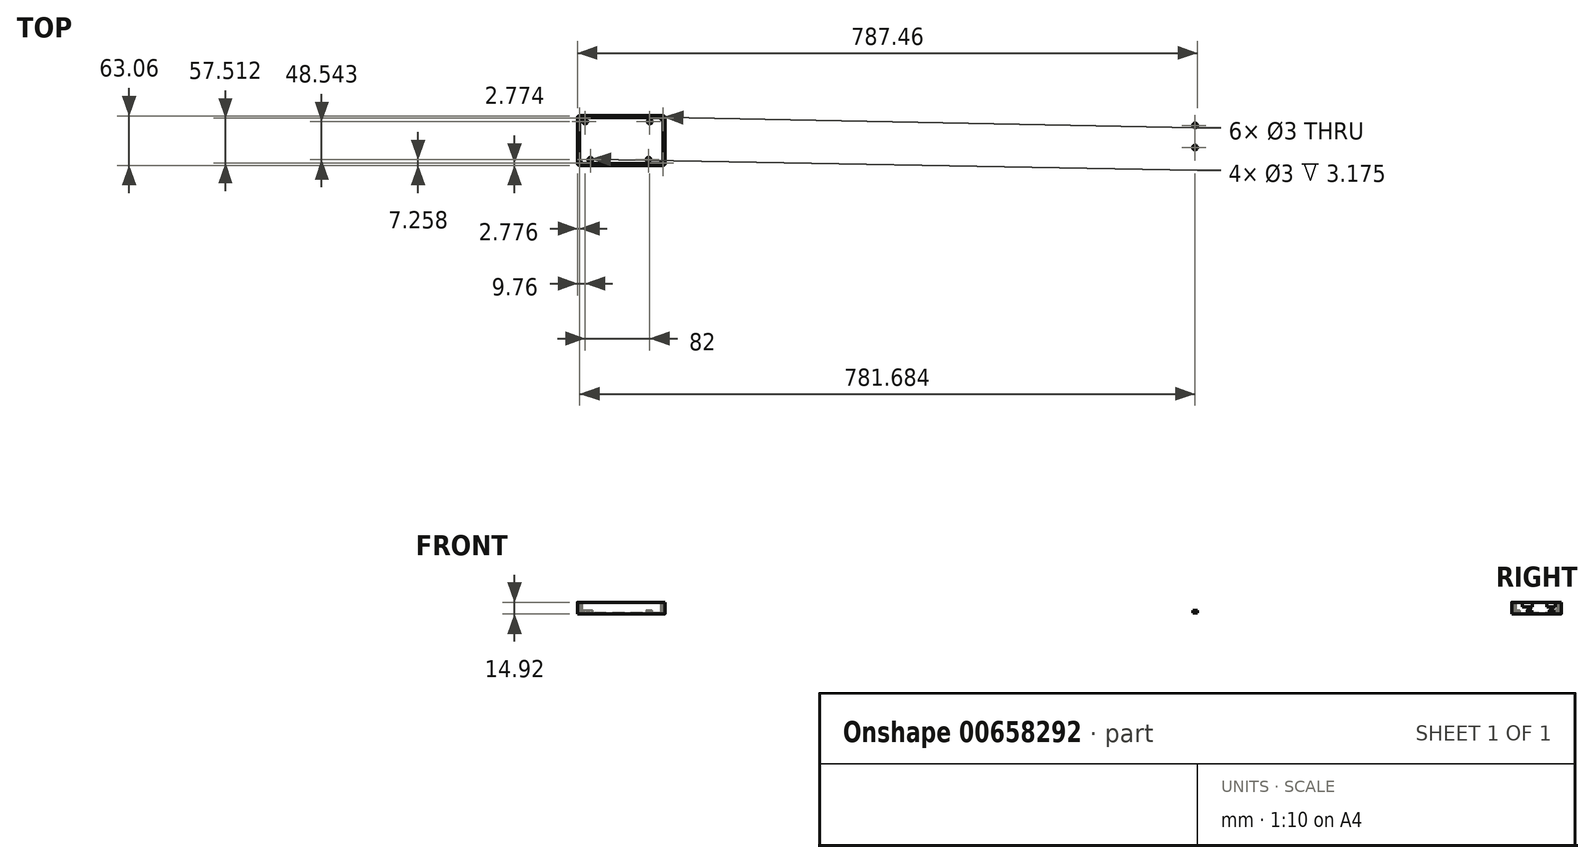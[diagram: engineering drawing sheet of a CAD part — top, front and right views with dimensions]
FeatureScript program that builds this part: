
annotation { "Feature Type Name" : "Feature", "Feature Type Description" : "" }
export const myFeature = defineFeature(function(context is Context, id is Id, definition is map)
    precondition{}
    {
        {
            var Q0;
            Q0=qCreatedBy(makeId("Top.planeOp"),FACE);
            var sketch = newSketch(context, id + "F0", { "sketchPlane" : qUnion([Q0])});
            skLineSegment(sketch, "E0.bottom", {"start": v(50.8, 26.77) * mm, "end": v(-50.8, 26.77) * mm});
            skLineSegment(sketch, "E0.top", {"start": v(50.8, -26.77) * mm, "end": v(-50.8, -26.77) * mm});
            skLineSegment(sketch, "E0.left", {"start": v(50.8, 26.77) * mm, "end": v(50.8, -26.77) * mm});
            skLineSegment(sketch, "E0.right", {"start": v(-50.8, 26.77) * mm, "end": v(-50.8, -26.77) * mm});
            skPoint(sketch, "E0.middle", {"position": v(0, 0) * mm});
            skSolve(sketch);
        }
        {
            var Q0;
            Q0=qCreatedBy(makeId("Top.planeOp"),FACE);
            var sketch = newSketch(context, id + "F1", { "sketchPlane" : qUnion([Q0])});
            skLineSegment(sketch, "E1.bottom", {"start": v(55.56, 31.53) * mm, "end": v(-55.56, 31.53) * mm});
            skLineSegment(sketch, "E1.top", {"start": v(55.56, -31.53) * mm, "end": v(-55.56, -31.53) * mm});
            skLineSegment(sketch, "E1.left", {"start": v(55.56, 31.53) * mm, "end": v(55.56, -31.53) * mm});
            skLineSegment(sketch, "E1.right", {"start": v(-55.56, 31.53) * mm, "end": v(-55.56, -31.53) * mm});
            skPoint(sketch, "E1.middle", {"position": v(0, 0) * mm});
            skLineSegment(sketch, "E2.bottom", {"start": v(53.97, 29.95) * mm, "end": v(-53.98, 29.95) * mm, "construction": true});
            skLineSegment(sketch, "E2.top", {"start": v(53.98, -29.95) * mm, "end": v(-53.97, -29.95) * mm, "construction": true});
            skLineSegment(sketch, "E2.left", {"start": v(53.97, 29.95) * mm, "end": v(53.98, -29.95) * mm, "construction": true});
            skLineSegment(sketch, "E2.right", {"start": v(-53.98, 29.95) * mm, "end": v(-53.97, -29.95) * mm, "construction": true});
            skSolve(sketch);
        }
        {
            var Q0;
            Q0=makeQuery(id+"F1.imprint","IMPRINT",FACE,{"disambiguationData":[TD([[makeQuery(id+"F1.imprint","IMPRINT",EDGE,{"derivedFrom":sQuery(id+"F1.wireOp",EDGE,"E1.bottom")}),1.0]])]});
            extrude(context, id + "F2", {"entities" : qUnion([Q0]), "depth" : 1.59 * mm, "offsetDistance" : 25.4 * mm});
        }
        {
            var Q0;
            Q0=makeQuery(id+"F2.opExtrude","CAP_FACE",FACE,{"disambiguationData":[OSD([sQuery(id+"F1.wireOp",EDGE,"E1.bottom"),sQuery(id+"F1.wireOp",EDGE,"E1.top"),sQuery(id+"F1.wireOp",EDGE,"E1.left"),sQuery(id+"F1.wireOp",EDGE,"E1.right")])],"isStart":false});
            var sketch = newSketch(context, id + "F3", { "sketchPlane" : qUnion([Q0])});
            skLineSegment(sketch, "E3.bottom", {"start": v(55.56, 31.53) * mm, "end": v(-55.56, 31.53) * mm});
            skLineSegment(sketch, "E3.top", {"start": v(55.56, -31.53) * mm, "end": v(-55.56, -31.53) * mm});
            skLineSegment(sketch, "E3.left", {"start": v(55.56, 31.53) * mm, "end": v(55.56, -31.53) * mm});
            skLineSegment(sketch, "E3.right", {"start": v(-55.56, 31.53) * mm, "end": v(-55.56, -31.53) * mm});
            skPoint(sketch, "E3.middle", {"position": v(0, 0) * mm});
            skLineSegment(sketch, "E4.left", {"start": v(53.18, 25.98) * mm, "end": v(53.18, -25.98) * mm});
            skLineSegment(sketch, "E4.right", {"start": v(-53.18, 25.98) * mm, "end": v(-53.18, -25.98) * mm});
            skArc(sketch, "E5", {"start": v(-52.78, 25.98) * mm, "mid": v(-50.82, 26.8) * mm, "end": v(-50, 28.76) * mm});
            skCircle(sketch, "E6", {"center": v(-52.78, 28.76) * mm, "radius": 1.5 * mm});
            skLineSegment(sketch, "E7", {"start": v(-50, 28.76) * mm, "end": v(-50, 29.15) * mm});
            skLineSegment(sketch, "E8", {"start": v(-52.78, 25.98) * mm, "end": v(-53.18, 25.98) * mm});
            skLineSegment(sketch, "E9", {"start": v(-55.56, 31.53) * mm, "end": v(-50.82, 26.8) * mm, "construction": true});
            skPoint(sketch, "E10", {"position": v(-53.2, 29.16) * mm});
            skPoint(sketch, "E11.orphan", {"position": v(-53.18, 37.1) * mm});
            skCircle(sketch, "E12.MirrorC", {"center": v(-52.78, -28.76) * mm, "radius": 1.5 * mm});
            skLineSegment(sketch, "E13.MirrorCS", {"start": v(-52.78, -25.98) * mm, "end": v(-53.18, -25.98) * mm});
            skArc(sketch, "E14.MirrorCS", {"start": v(-52.78, -25.98) * mm, "mid": v(-50.82, -26.8) * mm, "end": v(-50, -28.76) * mm});
            skLineSegment(sketch, "E15.MirrorCS", {"start": v(-50, -28.76) * mm, "end": v(-50, -29.15) * mm});
            skCircle(sketch, "E16.MirrorC", {"center": v(52.78, 28.76) * mm, "radius": 1.5 * mm});
            skLineSegment(sketch, "E17.MirrorCS", {"start": v(50, 28.76) * mm, "end": v(50, 29.15) * mm});
            skArc(sketch, "E18.MirrorCS", {"start": v(52.78, 25.98) * mm, "mid": v(50.82, 26.8) * mm, "end": v(50, 28.76) * mm});
            skLineSegment(sketch, "E19.MirrorCS", {"start": v(52.78, 25.98) * mm, "end": v(53.18, 25.98) * mm});
            skCircle(sketch, "E20.MirrorC", {"center": v(52.78, -28.76) * mm, "radius": 1.5 * mm});
            skLineSegment(sketch, "E21.MirrorCS", {"start": v(52.78, -25.98) * mm, "end": v(53.18, -25.98) * mm});
            skArc(sketch, "E22.MirrorCS", {"start": v(52.78, -25.98) * mm, "mid": v(50.82, -26.8) * mm, "end": v(50, -28.76) * mm});
            skLineSegment(sketch, "E23.MirrorCS", {"start": v(50, -28.76) * mm, "end": v(50, -29.15) * mm});
            skPoint(sketch, "E24.orphan", {"position": v(-53.18, -36.9) * mm});
            skLineSegment(sketch, "E25.trimOffspring", {"start": v(50, -29.15) * mm, "end": v(-50, -29.15) * mm});
            skPoint(sketch, "E26.orphan", {"position": v(53.18, -37.1) * mm});
            skLineSegment(sketch, "E27.trimOffspring", {"start": v(50, 29.15) * mm, "end": v(-50, 29.15) * mm});
            skPoint(sketch, "E28.orphan", {"position": v(53.18, 36.9) * mm});
            skSolve(sketch);
        }
        {
            var Q0;
            Q0=qSketchRegion(id+"F3",true);
            extrude(context, id + "F4", {"entities" : qUnion([Q0]), "operationType" : NewBodyOperationType.ADD, "depth" : 13.33 * mm, "offsetDistance" : 25.4 * mm});
        }
        {
            var Q0;
            Q0=makeQuery(id+"F4.boolean.opBoolean","MERGE",EDGE,{"derivedFrom":[makeQuery(id+"F2.opExtrude","SWEPT_EDGE",EDGE,{"disambiguationData":[OSD([sQuery(id+"F1.wireOp",EDGE,"E1.top"),sQuery(id+"F1.wireOp",EDGE,"E1.left")])]}),makeQuery(id+"F4.opExtrude","SWEPT_EDGE",EDGE,{"disambiguationData":[OSD([sQuery(id+"F3.wireOp",EDGE,"E3.top"),sQuery(id+"F3.wireOp",EDGE,"E3.left")])]})]});
            var Q1;
            Q1=makeQuery(id+"F4.boolean.opBoolean","MERGE",EDGE,{"derivedFrom":[makeQuery(id+"F2.opExtrude","SWEPT_EDGE",EDGE,{"disambiguationData":[OSD([sQuery(id+"F1.wireOp",EDGE,"E1.bottom"),sQuery(id+"F1.wireOp",EDGE,"E1.left")])]}),makeQuery(id+"F4.opExtrude","SWEPT_EDGE",EDGE,{"disambiguationData":[OSD([sQuery(id+"F3.wireOp",EDGE,"E3.bottom"),sQuery(id+"F3.wireOp",EDGE,"E3.left")])]})]});
            var Q2;
            Q2=makeQuery(id+"F4.boolean.opBoolean","MERGE",EDGE,{"derivedFrom":[makeQuery(id+"F2.opExtrude","SWEPT_EDGE",EDGE,{"disambiguationData":[OSD([sQuery(id+"F1.wireOp",EDGE,"E1.top"),sQuery(id+"F1.wireOp",EDGE,"E1.right")])]}),makeQuery(id+"F4.opExtrude","SWEPT_EDGE",EDGE,{"disambiguationData":[OSD([sQuery(id+"F3.wireOp",EDGE,"E3.top"),sQuery(id+"F3.wireOp",EDGE,"E3.right")])]})]});
            var Q3;
            Q3=makeQuery(id+"F4.boolean.opBoolean","MERGE",EDGE,{"derivedFrom":[makeQuery(id+"F2.opExtrude","SWEPT_EDGE",EDGE,{"disambiguationData":[OSD([sQuery(id+"F1.wireOp",EDGE,"E1.bottom"),sQuery(id+"F1.wireOp",EDGE,"E1.right")])]}),makeQuery(id+"F4.opExtrude","SWEPT_EDGE",EDGE,{"disambiguationData":[OSD([sQuery(id+"F3.wireOp",EDGE,"E3.bottom"),sQuery(id+"F3.wireOp",EDGE,"E3.right")])]})]});
            fillet(context, id + "F5", {"entities" : qUnion([Q0, Q1, Q2, Q3]), "radius" : 2.38 * mm, "tangentPropagation" : true, "allowEdgeOverflow" : false});
        }
        {
            var Q0;
            Q0=makeQuery(id+"F4.boolean.opBoolean","MERGE",FACE,{"derivedFrom":[makeQuery(id+"F2.opExtrude","SWEPT_FACE",FACE,{"disambiguationData":[OSD([sQuery(id+"F1.wireOp",EDGE,"E1.left")])]}),makeQuery(id+"F4.opExtrude","SWEPT_FACE",FACE,{"disambiguationData":[OSD([sQuery(id+"F3.wireOp",EDGE,"E3.left")])]})]});
            var sketch = newSketch(context, id + "F6", { "sketchPlane" : qUnion([Q0])});
            skLineSegment(sketch, "E29.bottom", {"start": v(-18.02, 14.92) * mm, "end": v(-5.52, 14.92) * mm});
            skLineSegment(sketch, "E29.top", {"start": v(-18.02, 9.4) * mm, "end": v(-5.52, 9.4) * mm});
            skLineSegment(sketch, "E29.left", {"start": v(-18.02, 14.92) * mm, "end": v(-18.02, 9.4) * mm});
            skLineSegment(sketch, "E29.right", {"start": v(-5.52, 14.92) * mm, "end": v(-5.52, 9.4) * mm});
            skLineSegment(sketch, "E30.bottom", {"start": v(13.27, 14.92) * mm, "end": v(23.77, 14.92) * mm});
            skLineSegment(sketch, "E30.top", {"start": v(13.27, 9.4) * mm, "end": v(23.77, 9.4) * mm});
            skLineSegment(sketch, "E30.left", {"start": v(13.27, 14.92) * mm, "end": v(13.27, 9.4) * mm});
            skLineSegment(sketch, "E30.right", {"start": v(23.77, 14.92) * mm, "end": v(23.77, 9.4) * mm});
            skPoint(sketch, "E31", {"position": v(-11.77, 9.4) * mm});
            skPoint(sketch, "E32", {"position": v(18.52, 9.4) * mm});
            skLineSegment(sketch, "E33", {"start": v(-26.77, 14.92) * mm, "end": v(-26.77, 0) * mm, "construction": true});
            skLineSegment(sketch, "E34.MirrorCS", {"start": v(26.77, 14.92) * mm, "end": v(26.77, 0) * mm, "construction": true});
            skSolve(sketch);
        }
        {
            var Q0;
            Q0=qSketchRegion(id+"F6",true);
            extrude(context, id + "F7", {"entities" : qUnion([Q0]), "operationType" : NewBodyOperationType.REMOVE, "endBound" : BoundingType.UP_TO_NEXT, "oppositeDirection" : true, "depth" : 25.4 * mm, "offsetDistance" : 25.4 * mm});
        }
        {
            var Q0;
            Q0=makeQuery(id+"F4.boolean.opBoolean","SPLIT",FACE,{"disambiguationData":[TD([makeQuery(id+"F4.opExtrude","SWEPT_FACE",FACE,{"disambiguationData":[OSD([sQuery(id+"F3.wireOp",EDGE,"E4.left")])]})])],"derivedFrom":makeQuery(id+"F2.opExtrude","CAP_FACE",FACE,{"disambiguationData":[OSD([sQuery(id+"F1.wireOp",EDGE,"E1.bottom"),sQuery(id+"F1.wireOp",EDGE,"E1.top"),sQuery(id+"F1.wireOp",EDGE,"E1.left"),sQuery(id+"F1.wireOp",EDGE,"E1.right")])],"isStart":false})});
            var sketch = newSketch(context, id + "F8", { "sketchPlane" : qUnion([Q0])});
            skCircle(sketch, "E35", {"center": v(-45.8, 24.27) * mm, "radius": 1.5 * mm});
            skCircle(sketch, "E36", {"center": v(-39.3, -24.27) * mm, "radius": 1.5 * mm});
            skCircle(sketch, "E37", {"center": v(728.9, 19.27) * mm, "radius": 1.5 * mm});
            skCircle(sketch, "E38", {"center": v(728.9, -8.73) * mm, "radius": 1.5 * mm});
            skCircle(sketch, "E39", {"center": v(36.2, 24.27) * mm, "radius": 1.5 * mm});
            skCircle(sketch, "E40", {"center": v(34.7, -24.27) * mm, "radius": 1.5 * mm});
            skCircle(sketch, "E41", {"center": v(-45.8, 24.27) * mm, "radius": 3 * mm});
            skCircle(sketch, "E42", {"center": v(-39.3, -24.27) * mm, "radius": 3 * mm});
            skCircle(sketch, "E43", {"center": v(728.9, 19.27) * mm, "radius": 3 * mm});
            skCircle(sketch, "E44", {"center": v(728.9, -8.73) * mm, "radius": 3 * mm});
            skCircle(sketch, "E45", {"center": v(36.2, 24.27) * mm, "radius": 3 * mm});
            skCircle(sketch, "E46", {"center": v(34.7, -24.27) * mm, "radius": 3 * mm});
            skSolve(sketch);
        }
        {
            var Q0;
            Q0=qSketchRegion(id+"F8",true);
            extrude(context, id + "F9", {"entities" : qUnion([Q0]), "operationType" : NewBodyOperationType.ADD, "depth" : 3.17 * mm, "offsetDistance" : 25.4 * mm});
        }
        {
            var Q0;
            {var subQ0=sQuery(id+"F3.wireOp",EDGE,"E18.MirrorCS");var subQ1=sQuery(id+"F3.wireOp",EDGE,"E17.MirrorCS");var subQ2=sQuery(id+"F3.wireOp",EDGE,"E16.MirrorC");var subQ3=sQuery(id+"F3.wireOp",EDGE,"E15.MirrorCS");var subQ4=sQuery(id+"F3.wireOp",EDGE,"E14.MirrorCS");var subQ5=sQuery(id+"F3.wireOp",EDGE,"E13.MirrorCS");var subQ6=sQuery(id+"F3.wireOp",EDGE,"E12.MirrorC");var subQ7=sQuery(id+"F3.wireOp",EDGE,"E8");var subQ8=sQuery(id+"F3.wireOp",EDGE,"E7");var subQ9=sQuery(id+"F3.wireOp",EDGE,"E6");var subQ10=sQuery(id+"F3.wireOp",EDGE,"E5");var subQ11=sQuery(id+"F3.wireOp",EDGE,"E3.top");var subQ12=sQuery(id+"F3.wireOp",EDGE,"E3.left");var subQ13=sQuery(id+"F3.wireOp",EDGE,"E3.bottom");var subQ15=sQuery(id+"F1.wireOp",EDGE,"E1.bottom");var subQ17=sQuery(id+"F3.wireOp",EDGE,"E22.MirrorCS");var subQ19=sQuery(id+"F3.wireOp",EDGE,"E25.trimOffspring");var subQ20=sQuery(id+"F3.wireOp",EDGE,"E3.right");var subQ21=sQuery(id+"F3.wireOp",EDGE,"E19.MirrorCS");var subQ22=sQuery(id+"F3.wireOp",EDGE,"E23.MirrorCS");var subQ23=sQuery(id+"F3.wireOp",EDGE,"E4.left");var subQ24=sQuery(id+"F3.wireOp",EDGE,"E4.right");var subQ25=sQuery(id+"F3.wireOp",EDGE,"E20.MirrorC");var subQ26=sQuery(id+"F3.wireOp",EDGE,"E21.MirrorCS");var subQ27=sQuery(id+"F3.wireOp",EDGE,"E27.trimOffspring");Q0=makeQuery(id+"F7.boolean.opBoolean","SPLIT",FACE,{"disambiguationData":[TD([makeQuery(id+"F2.opExtrude","SWEPT_FACE",FACE,{"disambiguationData":[OSD([subQ15])]})])],"derivedFrom":makeQuery(id+"F4.opExtrude","CAP_FACE",FACE,{"disambiguationData":[OSD([subQ13,subQ11,subQ12,subQ20,subQ23,subQ24,subQ10,subQ9,subQ8,subQ7,subQ6,subQ5,subQ4,subQ3,subQ2,subQ1,subQ0,subQ21,subQ25,subQ26,subQ17,subQ22,subQ19,subQ27])],"isStart":false})});}
            var sketch = newSketch(context, id + "F10", { "sketchPlane" : qUnion([Q0])});
            skCircle(sketch, "E47.0", {"center": v(-52.78, 28.76) * mm, "radius": 1.5 * mm});
            skCircle(sketch, "E48.0", {"center": v(-52.78, -28.76) * mm, "radius": 1.5 * mm});
            skCircle(sketch, "E49.0", {"center": v(52.78, -28.76) * mm, "radius": 1.5 * mm});
            skCircle(sketch, "E50.0", {"center": v(52.78, 28.76) * mm, "radius": 1.5 * mm});
            skSolve(sketch);
        }
        {
            var Q0;
            Q0=qSketchRegion(id+"F10",true);
            extrude(context, id + "F11", {"entities" : qUnion([Q0]), "operationType" : NewBodyOperationType.REMOVE, "endBound" : BoundingType.THROUGH_ALL, "oppositeDirection" : true, "depth" : 25.4 * mm, "offsetDistance" : 25.4 * mm});
        }
    });
